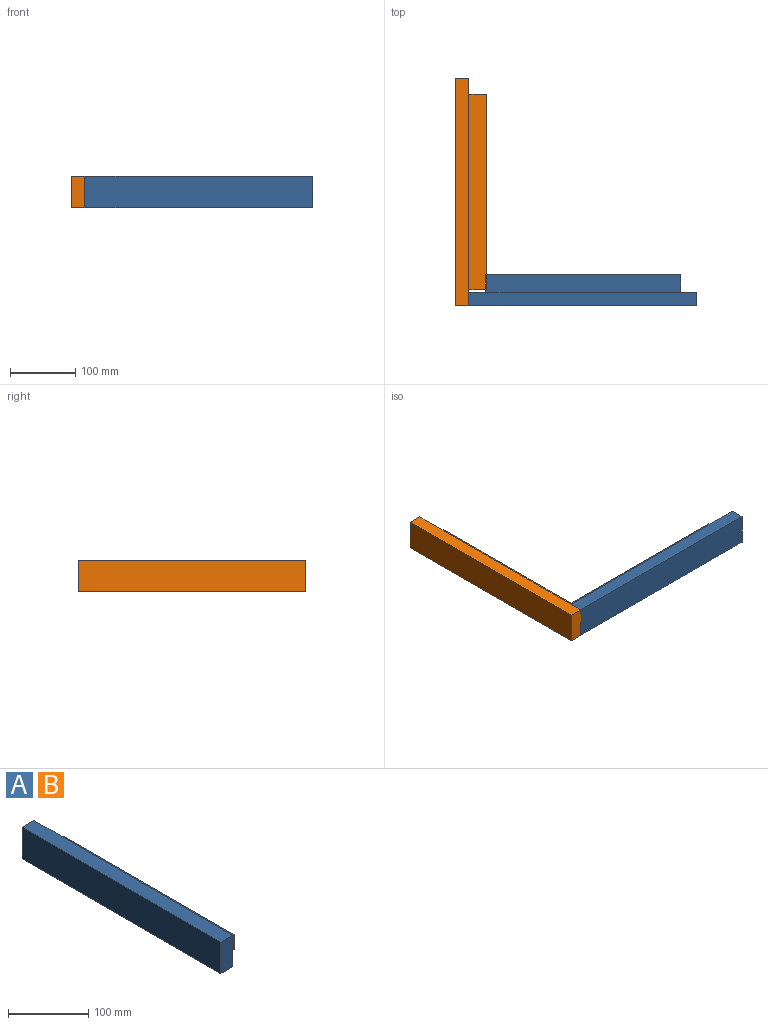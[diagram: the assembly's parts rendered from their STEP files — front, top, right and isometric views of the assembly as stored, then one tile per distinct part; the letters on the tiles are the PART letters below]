
ASSEMBLY  parts=2 mates=1
PART A: 10 faces, bbox 48x350x48 mm
  f0: plane 300x23mm, normal (1,0,0), area 6900mm2, adj f1,f3,f8,f9
  f1: plane 300x27mm, normal (0,0,1), area 8100mm2, adj f0,f4,f8,f9
  f2: plane 350x48mm, normal (-1,0,0), area 16800mm2, adj f3,f5,f6,f7
  f3: plane 350x48mm, normal (0,0,-1), area 15450mm2, adj f0,f2,f4,f6,f7,f8,f9
  f4: plane 350x48mm, normal (1,0,0), area 9900mm2, adj f1,f3,f5,f6,f7,f8,f9
  f5: plane 350x21mm, normal (0,0,1), area 7350mm2, adj f2,f4,f6,f7
  f6: plane 48x21mm, normal (0,-1,0), area 1008mm2, adj f2,f3,f4,f5
  f7: plane 48x21mm, normal (0,1,0), area 1008mm2, adj f2,f3,f4,f5
  f8: plane 27x23mm, normal (0,-1,0), area 621mm2, adj f0,f1,f3,f4
  f9: plane 27x23mm, normal (0,1,0), area 621mm2, adj f0,f1,f3,f4
PART B: same geometry as A
PLACE A rot(axis=(0,0,1),90deg) t=(-129.41,-326.47,-45.16)mm
PLACE B t=(-150.41,23.53,-45.16)mm
MATE fastened B.f3 <-> A.f3  axis (0,0,-1) through (-129.41,-326.47,-45.16)mm
